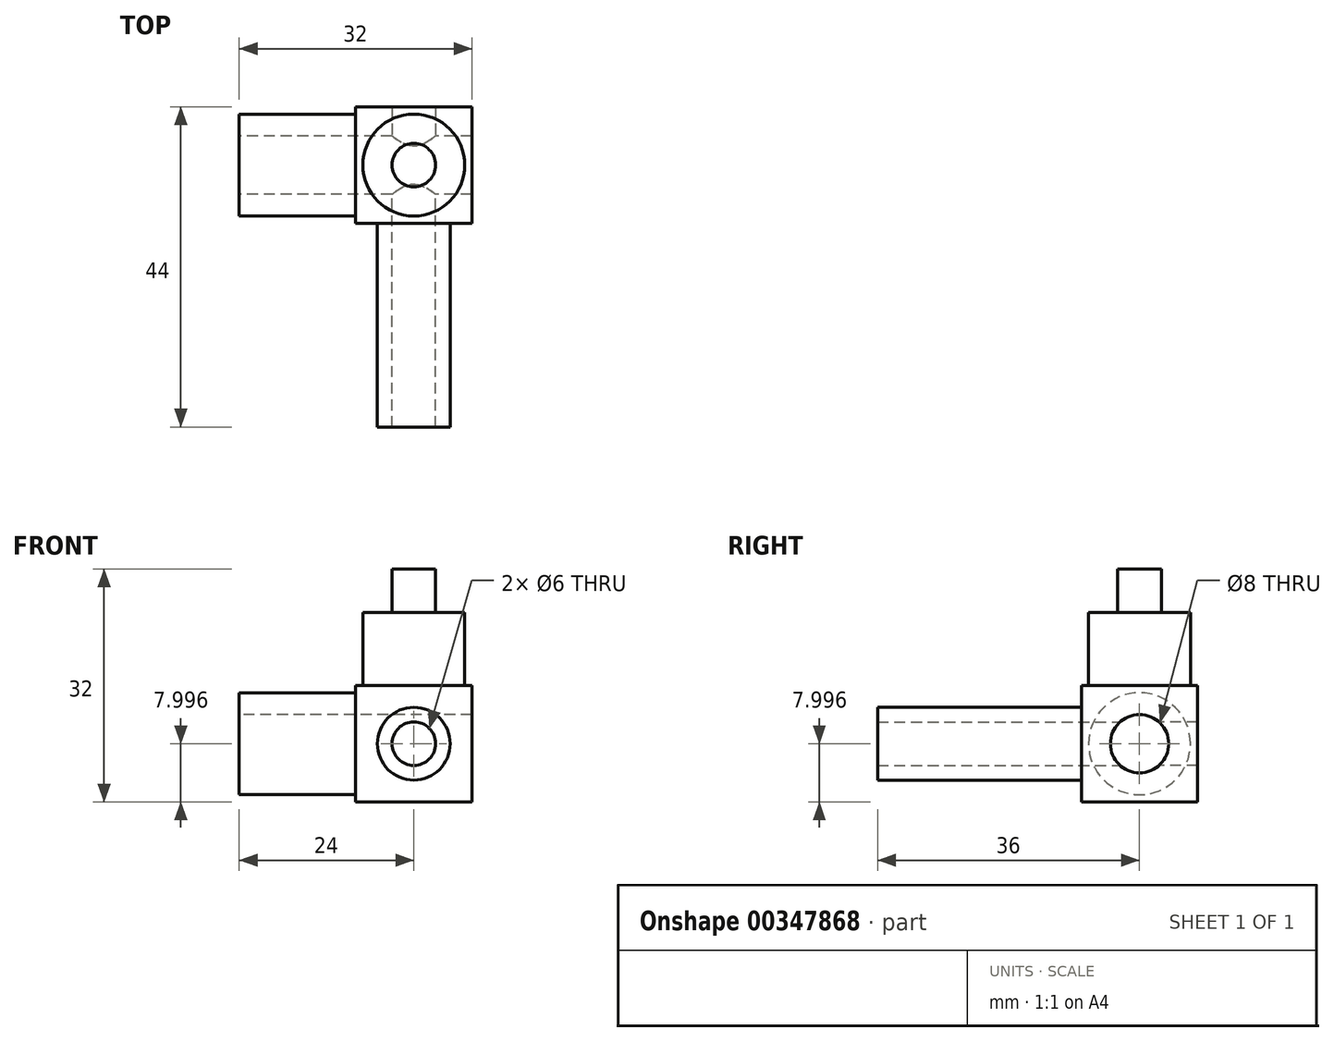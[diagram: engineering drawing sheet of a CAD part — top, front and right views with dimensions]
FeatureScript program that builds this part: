
annotation { "Feature Type Name" : "Feature", "Feature Type Description" : "" }
export const myFeature = defineFeature(function(context is Context, id is Id, definition is map)
    precondition{}
    {
        {
            var Q0;
            Q0=qCreatedBy(makeId("Front.planeOp"),FACE);
            var sketch = newSketch(context, id + "F0", { "sketchPlane" : qUnion([Q0])});
            skLineSegment(sketch, "E0", {"start": v(-26.19, -2.7) * mm, "end": v(16.37, -2.7) * mm, "construction": true});
            skLineSegment(sketch, "E1", {"start": v(0, 22.2) * mm, "end": v(0, -14.23) * mm, "construction": true});
            skLineSegment(sketch, "E2", {"start": v(8, -2.7) * mm, "end": v(8, 5.3) * mm});
            skLineSegment(sketch, "E3.MirrorCS", {"start": v(8, -2.7) * mm, "end": v(8, -10.7) * mm});
            skLineSegment(sketch, "E4.MirrorCS", {"start": v(-8, -2.7) * mm, "end": v(-8, -10.7) * mm});
            skLineSegment(sketch, "E5.MirrorCS", {"start": v(-8, -2.7) * mm, "end": v(-8, 5.3) * mm});
            skLineSegment(sketch, "E6", {"start": v(-8, 5.3) * mm, "end": v(8, 5.3) * mm});
            skLineSegment(sketch, "E7", {"start": v(8, -10.7) * mm, "end": v(-8, -10.7) * mm});
            skLineSegment(sketch, "E8", {"start": v(7, 5.3) * mm, "end": v(7, 15.3) * mm});
            skLineSegment(sketch, "E9", {"start": v(7, 15.3) * mm, "end": v(-7, 15.3) * mm});
            skLineSegment(sketch, "E10", {"start": v(-7, 15.3) * mm, "end": v(-7, 5.3) * mm});
            skLineSegment(sketch, "E11", {"start": v(-3, 15.3) * mm, "end": v(-3, 21.3) * mm});
            skLineSegment(sketch, "E12", {"start": v(-3, 21.3) * mm, "end": v(3, 21.3) * mm});
            skLineSegment(sketch, "E13", {"start": v(3, 21.3) * mm, "end": v(3, 15.3) * mm});
            skLineSegment(sketch, "E14", {"start": v(-8, 4) * mm, "end": v(-24, 4) * mm});
            skPoint(sketch, "E14.endSnap0", {"position": v(-8, 4.3) * mm});
            skLineSegment(sketch, "E15", {"start": v(-24, 4) * mm, "end": v(-24, -10) * mm});
            skLineSegment(sketch, "E16", {"start": v(-24, -9.7) * mm, "end": v(-8, -9.7) * mm});
            skPoint(sketch, "E17", {"position": v(0, 21.3) * mm});
            skLineSegment(sketch, "E18", {"start": v(0, 5.3) * mm, "end": v(0, 15.3) * mm});
            skLineSegment(sketch, "E19", {"start": v(0, 15.3) * mm, "end": v(0, 21.3) * mm});
            skLineSegment(sketch, "E20", {"start": v(-8, -2.7) * mm, "end": v(-24, -2.7) * mm});
            skSolve(sketch);
        }
        {
            var Q0;
            {var subQ5=sQuery(id+"F0.wireOp",EDGE,"E2");Q0=makeQuery(id+"F0.imprint","IMPRINT",FACE,{"disambiguationData":[TD([[makeQuery(id+"F0.imprint","IMPRINT",EDGE,{"derivedFrom":subQ5}),1.0]])]});}
            extrude(context, id + "F1", {"entities" : qUnion([Q0]), "depth" : 8 * mm});
        }
        {
            var Q0;
            Q0=makeQuery(id+"F1.opExtrude","CAP_FACE",FACE,{"disambiguationData":[OSD([sQuery(id+"F0.wireOp",EDGE,"E2"),sQuery(id+"F0.wireOp",EDGE,"E3.MirrorCS"),sQuery(id+"F0.wireOp",EDGE,"E4.MirrorCS"),sQuery(id+"F0.wireOp",EDGE,"E5.MirrorCS"),sQuery(id+"F0.wireOp",EDGE,"E6"),sQuery(id+"F0.wireOp",EDGE,"E7")])],"isStart":true});
            extrude(context, id + "F2", {"entities" : qUnion([Q0]), "operationType" : NewBodyOperationType.ADD, "depth" : 8 * mm});
        }
        {
            var Q0;
            {var subQ0=sQuery(id+"F0.wireOp",EDGE,"E11");Q0=makeQuery(id+"F0.imprint","IMPRINT",FACE,{"disambiguationData":[TD([[makeQuery(id+"F0.imprint","IMPRINT",EDGE,{"derivedFrom":subQ0}),-1.0]])]});}
            var Q1;
            {var subQ0=sQuery(id+"F0.wireOp",EDGE,"E10");Q1=makeQuery(id+"F0.imprint","IMPRINT",FACE,{"disambiguationData":[TD([[makeQuery(id+"F0.imprint","IMPRINT",EDGE,{"derivedFrom":subQ0}),1.0]])]});}
            var Q2;
            Q2=sQuery(id+"F0.wireOp",EDGE,"E19");
            revolve(context, id + "F3", {"operationType" : NewBodyOperationType.ADD, "entities" : qUnion([Q0, Q1]), "axis" : qUnion([Q2]), "revolveType" : RevolveType.FULL});
        }
        {
            var Q0;
            {var subQ2=sQuery(id+"F0.wireOp",EDGE,"E16");Q0=makeQuery(id+"F0.imprint","IMPRINT",FACE,{"disambiguationData":[TD([[makeQuery(id+"F0.imprint","IMPRINT",EDGE,{"derivedFrom":subQ2}),1.0]])]});}
            var Q1;
            Q1=sQuery(id+"F0.wireOp",EDGE,"E20");
            revolve(context, id + "F4", {"operationType" : NewBodyOperationType.ADD, "entities" : qUnion([Q0]), "axis" : qUnion([Q1]), "revolveType" : RevolveType.FULL});
        }
        {
            var Q0;
            Q0=makeQuery(id+"F4.opRevolve","SWEPT_FACE",FACE,{"disambiguationData":[OSD([sQuery(id+"F0.wireOp",EDGE,"E15")])]});
            var sketch = newSketch(context, id + "F5", { "sketchPlane" : qUnion([Q0])});
            skCircle(sketch, "E21", {"center": v(0, -2.7) * mm, "radius": 4 * mm});
            skSolve(sketch);
        }
        {
            var Q0;
            Q0=makeQuery(id+"F5.imprint","IMPRINT",FACE,{"disambiguationData":[TD([[makeQuery(id+"F5.imprint","IMPRINT",EDGE,{"derivedFrom":sQuery(id+"F5.wireOp",EDGE,"E21")}),1.0]])]});
            extrude(context, id + "F6", {"entities" : qUnion([Q0]), "operationType" : NewBodyOperationType.REMOVE, "oppositeDirection" : true, "depth" : 37 * mm});
        }
        {
            var Q0;
            Q0=makeQuery(id+"F1.opExtrude","CAP_FACE",FACE,{"disambiguationData":[OSD([sQuery(id+"F0.wireOp",EDGE,"E2"),sQuery(id+"F0.wireOp",EDGE,"E3.MirrorCS"),sQuery(id+"F0.wireOp",EDGE,"E4.MirrorCS"),sQuery(id+"F0.wireOp",EDGE,"E5.MirrorCS"),sQuery(id+"F0.wireOp",EDGE,"E6"),sQuery(id+"F0.wireOp",EDGE,"E7")])],"isStart":false});
            var sketch = newSketch(context, id + "F7", { "sketchPlane" : qUnion([Q0])});
            skLineSegment(sketch, "E22", {"start": v(-8, 5.3) * mm, "end": v(8, -10.7) * mm, "construction": true});
            skLineSegment(sketch, "E23", {"start": v(8, -10.7) * mm, "end": v(-8, -10.7) * mm, "construction": true});
            skLineSegment(sketch, "E24", {"start": v(-8, -10.7) * mm, "end": v(8, 5.3) * mm, "construction": true});
            skCircle(sketch, "E25", {"center": v(0, -2.7) * mm, "radius": 5 * mm});
            skCircle(sketch, "E26", {"center": v(0, -2.7) * mm, "radius": 3 * mm});
            skSolve(sketch);
        }
        {
            var Q0;
            Q0=makeQuery(id+"F7.imprint","IMPRINT",FACE,{"disambiguationData":[TD([[makeQuery(id+"F7.imprint","IMPRINT",EDGE,{"derivedFrom":sQuery(id+"F7.wireOp",EDGE,"E25")}),1.0]])]});
            extrude(context, id + "F8", {"entities" : qUnion([Q0]), "operationType" : NewBodyOperationType.ADD, "depth" : (44 - 16) * mm});
        }
        {
            var Q0;
            Q0=makeQuery(id+"F8.boolean.opBoolean","SPLIT",FACE,{"disambiguationData":[TD([makeQuery(id+"F8.opExtrude","SWEPT_FACE",FACE,{"disambiguationData":[OSD([sQuery(id+"F7.wireOp",EDGE,"E26")])]})])],"derivedFrom":makeQuery(id+"F1.opExtrude","CAP_FACE",FACE,{"disambiguationData":[OSD([sQuery(id+"F0.wireOp",EDGE,"E2"),sQuery(id+"F0.wireOp",EDGE,"E3.MirrorCS"),sQuery(id+"F0.wireOp",EDGE,"E4.MirrorCS"),sQuery(id+"F0.wireOp",EDGE,"E5.MirrorCS"),sQuery(id+"F0.wireOp",EDGE,"E6"),sQuery(id+"F0.wireOp",EDGE,"E7")])],"isStart":false})});
            extrude(context, id + "F9", {"entities" : qUnion([Q0]), "operationType" : NewBodyOperationType.REMOVE, "oppositeDirection" : true, "depth" : 25 * mm});
        }
    });
